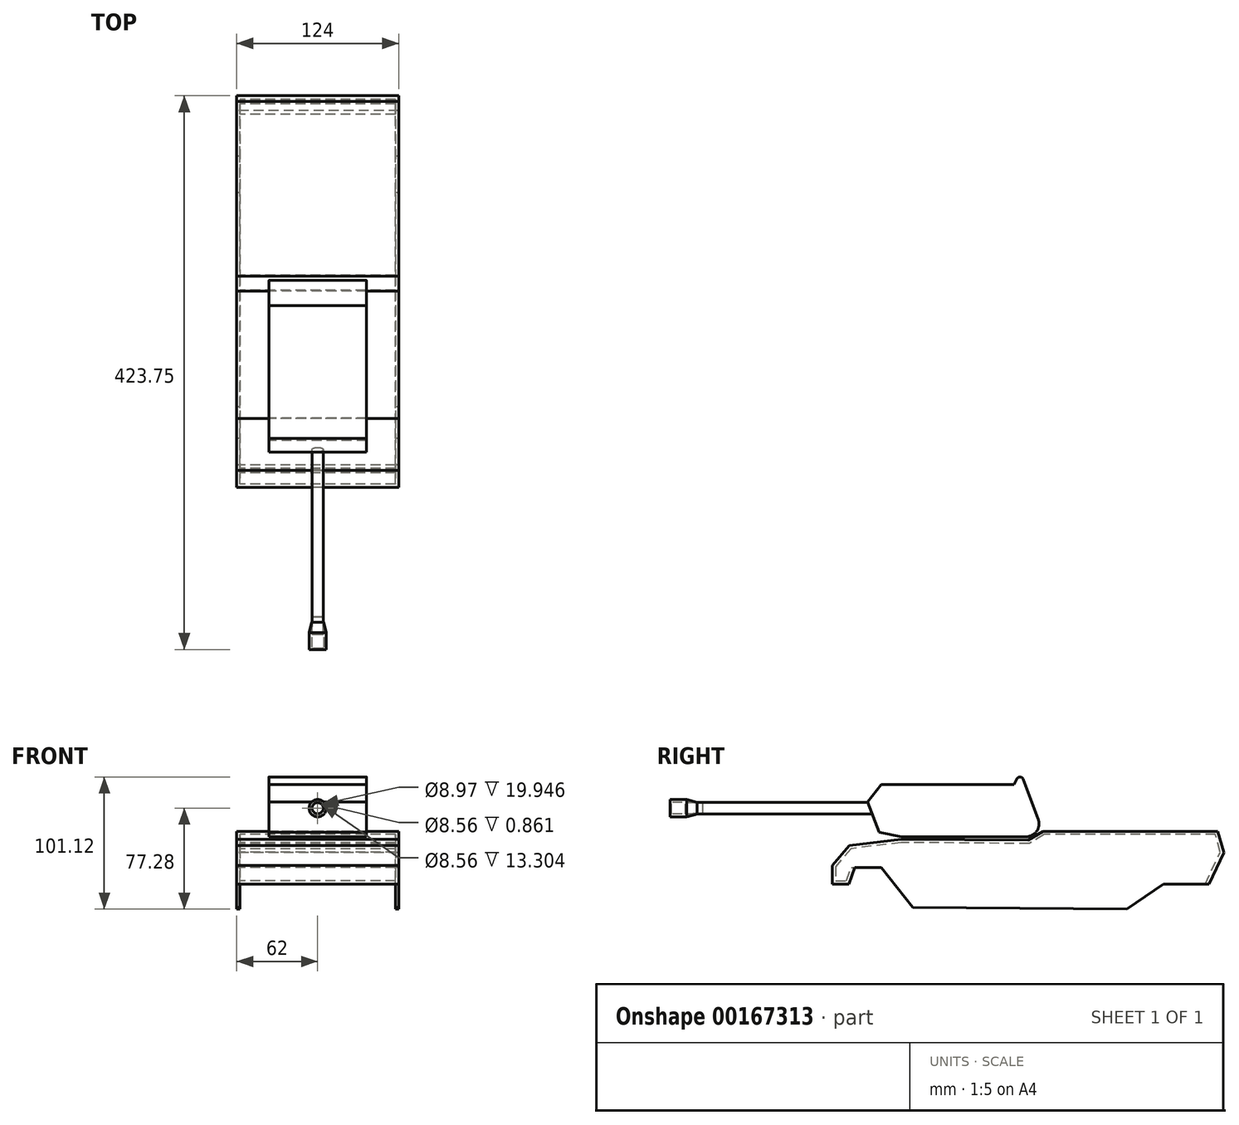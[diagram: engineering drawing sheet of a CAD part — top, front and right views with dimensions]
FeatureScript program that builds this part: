
annotation { "Feature Type Name" : "Feature", "Feature Type Description" : "" }
export const myFeature = defineFeature(function(context is Context, id is Id, definition is map)
    precondition{}
    {
        {
            var Q0;
            Q0=qCreatedBy(makeId("Front.planeOp"),FACE);
            var sketch = newSketch(context, id + "F0", { "sketchPlane" : qUnion([Q0])});
            skCircle(sketch, "E0", {"center": v(0, 0) * mm, "radius": 4.4 * mm});
            skSolve(sketch);
        }
        {
            var Q0;
            Q0 = qSketchRegion(id + "F0", true);
            extrude(context, id + "F1", {"entities" : qUnion([Q0]), "depth" : 150 * mm});
        }
        {
            var Q0;
            Q0=qCreatedBy(makeId("Top.planeOp"),FACE);
            var sketch = newSketch(context, id + "F2", { "sketchPlane" : qUnion([Q0])});
            skLineSegment(sketch, "E1", {"start": v(-4.49, -140.89) * mm, "end": v(-6.58, -148.87) * mm});
            skLineSegment(sketch, "E2", {"start": v(-6.58, -148.87) * mm, "end": v(-6.58, -161.7) * mm});
            skLineSegment(sketch, "E3", {"start": v(-6.58, -161.7) * mm, "end": v(0, -161.7) * mm});
            skLineSegment(sketch, "E4", {"start": v(0, -161.7) * mm, "end": v(0, -160.84) * mm});
            skLineSegment(sketch, "E5", {"start": v(0, -160.84) * mm, "end": v(-4.49, -160.84) * mm});
            skLineSegment(sketch, "E6", {"start": v(-4.49, -160.84) * mm, "end": v(-4.49, -140.89) * mm});
            skLineSegment(sketch, "E7", {"start": v(0, -161.7) * mm, "end": v(0, -153.1) * mm, "construction": true});
            skPoint(sketch, "E8.end.orphan", {"position": v(-6.58, -140.89) * mm});
            skSolve(sketch);
        }
        {
            var Q0;
            Q0=makeQuery(id+"F2.imprint","IMPRINT",FACE,{"disambiguationData":[TD([[makeQuery(id+"F2.imprint","IMPRINT",EDGE,{"derivedFrom":sQuery(id+"F2.wireOp",EDGE,"E1")}),1.0]])]});
            var Q1;
            Q1=sQuery(id+"F2.wireOp",EDGE,"E7");
            revolve(context, id + "F3", {"entities" : qUnion([Q0]), "axis" : qUnion([Q1]), "revolveType" : RevolveType.FULL});
        }
        {
            var Q0;
            Q0=makeQuery(id+"F3.opRevolve","SWEPT_FACE",FACE,{"disambiguationData":[OSD([sQuery(id+"F2.wireOp",EDGE,"E3")])]});
            var sketch = newSketch(context, id + "F4", { "sketchPlane" : qUnion([Q0])});
            skCircle(sketch, "E9", {"center": v(0, 0) * mm, "radius": 4.28 * mm});
            skSolve(sketch);
        }
        {
            var Q0;
            Q0 = qSketchRegion(id + "F4", true);
            extrude(context, id + "F5", {"entities" : qUnion([Q0]), "operationType" : NewBodyOperationType.REMOVE, "oppositeDirection" : true, "depth" : 25 * mm});
        }
        {
            var Q0;
            Q0=qCreatedBy(makeId("Right.planeOp"),FACE);
            var sketch = newSketch(context, id + "F6", { "sketchPlane" : qUnion([Q0])});
            skLineSegment(sketch, "E10", {"start": v(-10.65, 4.75) * mm, "end": v(0, 18) * mm});
            skLineSegment(sketch, "E11", {"start": v(0, 18) * mm, "end": v(101.44, 18) * mm});
            skLineSegment(sketch, "E12", {"start": v(103.74, 22.39) * mm, "end": v(101.44, 18) * mm});
            skLineSegment(sketch, "E13", {"start": v(120.06, -8.35) * mm, "end": v(108.69, 22.08) * mm});
            skLineSegment(sketch, "E14", {"start": v(110.7, -21.85) * mm, "end": v(15.4, -21.85) * mm});
            skLineSegment(sketch, "E15", {"start": v(-1.67, -18.4) * mm, "end": v(15.4, -21.85) * mm});
            skLineSegment(sketch, "E16", {"start": v(-1.67, -18.4) * mm, "end": v(-10.65, 4.75) * mm});
            skPoint(sketch, "E17.visualSharp", {"position": v(125.1, -21.85) * mm});
            skArc(sketch, "E18.filletArc", {"start": v(110.7, -21.85) * mm, "mid": v(118.91, -17.55) * mm, "end": v(120.06, -8.35) * mm});
            skPoint(sketch, "E19.visualSharp", {"position": v(106.56, 27.76) * mm});
            skArc(sketch, "E19.filletArc", {"start": v(108.69, 22.08) * mm, "mid": v(106.31, 23.84) * mm, "end": v(103.74, 22.39) * mm});
            skSolve(sketch);
        }
        {
            var Q0;
            Q0 = qSketchRegion(id + "F6", true);
            extrude(context, id + "F7", {"entities" : qUnion([Q0]), "operationType" : NewBodyOperationType.ADD, "endBound" : BoundingType.SYMMETRIC, "depth" : 74.8 * mm});
        }
        {
            var Q0;
            Q0=qCreatedBy(makeId("Right.planeOp"),FACE);
            var sketch = newSketch(context, id + "F8", { "sketchPlane" : qUnion([Q0])});
            skLineSegment(sketch, "E20", {"start": v(15.06, -23.74) * mm, "end": v(-24.48, -28.63) * mm});
            skLineSegment(sketch, "E21", {"start": v(-24.48, -28.63) * mm, "end": v(-37.52, -43.71) * mm});
            skLineSegment(sketch, "E22", {"start": v(-37.52, -43.71) * mm, "end": v(-37.52, -57.98) * mm});
            skLineSegment(sketch, "E23", {"start": v(-37.52, -57.98) * mm, "end": v(-24.88, -57.98) * mm});
            skLineSegment(sketch, "E24", {"start": v(250.63, -57.98) * mm, "end": v(262.05, -33.93) * mm});
            skLineSegment(sketch, "E25", {"start": v(262.05, -33.93) * mm, "end": v(257.56, -17.63) * mm});
            skLineSegment(sketch, "E26", {"start": v(257.56, -17.63) * mm, "end": v(123.88, -17.63) * mm});
            skLineSegment(sketch, "E27", {"start": v(123.88, -17.63) * mm, "end": v(112.47, -24.56) * mm});
            skLineSegment(sketch, "E28", {"start": v(112.47, -24.56) * mm, "end": v(15.06, -23.74) * mm});
            skLineSegment(sketch, "E29", {"start": v(-24.88, -57.98) * mm, "end": v(-20.4, -45.34) * mm});
            skLineSegment(sketch, "E30", {"start": v(-20.4, -45.34) * mm, "end": v(0, -45.51) * mm});
            skLineSegment(sketch, "E31", {"start": v(0, -45.51) * mm, "end": v(24.03, -75.9) * mm});
            skLineSegment(sketch, "E32", {"start": v(24.03, -75.9) * mm, "end": v(187.86, -77.28) * mm});
            skLineSegment(sketch, "E33", {"start": v(187.86, -77.28) * mm, "end": v(215.9, -57.98) * mm});
            skLineSegment(sketch, "E34.trimOffspring", {"start": v(215.9, -57.98) * mm, "end": v(250.63, -57.98) * mm});
            skSolve(sketch);
        }
        {
            var Q0;
            Q0 = qSketchRegion(id + "F8", true);
            extrude(context, id + "F9", {"entities" : qUnion([Q0]), "endBound" : BoundingType.SYMMETRIC, "depth" : 124 * mm});
        }
        {
            var Q0;
            Q0=makeQuery(id+"F9.opExtrude","SWEPT_FACE",FACE,{"disambiguationData":[OSD([sQuery(id+"F8.wireOp",EDGE,"E32")])]});
            var Q1;
            Q1=makeQuery(id+"F9.opExtrude","SWEPT_FACE",FACE,{"disambiguationData":[OSD([sQuery(id+"F8.wireOp",EDGE,"E33")])]});
            var Q2;
            Q2=makeQuery(id+"F9.opExtrude","SWEPT_FACE",FACE,{"disambiguationData":[OSD([sQuery(id+"F8.wireOp",EDGE,"E34.trimOffspring")])]});
            var Q3;
            Q3=makeQuery(id+"F9.opExtrude","SWEPT_FACE",FACE,{"disambiguationData":[OSD([sQuery(id+"F8.wireOp",EDGE,"E31")])]});
            var Q4;
            Q4=makeQuery(id+"F9.opExtrude","SWEPT_FACE",FACE,{"disambiguationData":[OSD([sQuery(id+"F8.wireOp",EDGE,"E30")])]});
            shell(context, id + "F10", {"entities" : qUnion([Q0, Q1, Q2, Q3, Q4]), "thickness" : 2.5 * mm});
        }
    });
